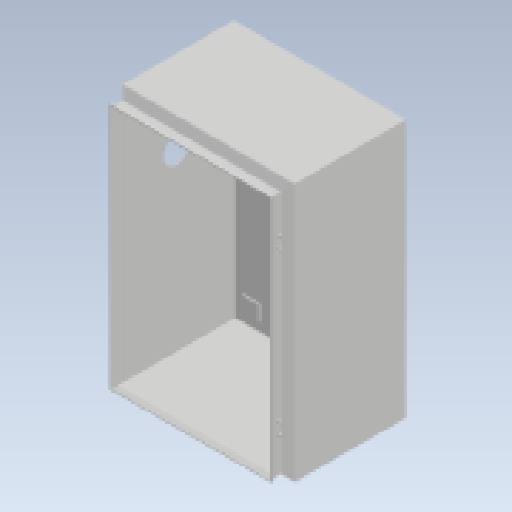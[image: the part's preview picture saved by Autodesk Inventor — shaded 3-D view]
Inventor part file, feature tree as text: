
AUTODESK INVENTOR PART (.ipt)
format: ipt  version: 2025.2 (Build 292293000, 293)  size: 891,392 bytes
history: native  units: mm
features: other x56, sketch x45, extrude x21, revolve x20, hole x4
ambient origin geometry x8: Origin, YZ Plane, XZ Plane, XY Plane, X Axis, Y Axis, Z Axis, Center Point
bodies: Solid1 (feature_tree)
feature tree (146):
  extrude  "Extrusion1"  Depth=300.0mm TaperAngle=0.0deg
  extrude  "Extrusion2"  Depth=300.0mm TaperAngle=0.0deg
  extrude  "Extrusion3"  Depth=3.25mm TaperAngle=0.0deg
  extrude  "Extrusion4"  Depth=3.25mm TaperAngle=0.0deg
  extrude  "Extrusion5"  Depth=15.297mm TaperAngle=0.0deg
  extrude  "Extrusion6"  Depth=15.297mm TaperAngle=0.0deg
  extrude  "Extrusion7"  Depth=15.297mm TaperAngle=0.0deg
  extrude  "Extrusion8"  Depth=15.297mm TaperAngle=0.0deg
  extrude  "Extrusion9"  TaperAngle=90.0deg  [1 undecoded]
  extrude  "Extrusion10"  TaperAngle=90.0deg  [1 undecoded]
  extrude  "Extrusion11"  TaperAngle=90.0deg  [1 undecoded]
  extrude  "Extrusion12"  TaperAngle=90.0deg  [1 undecoded]
  extrude  "Extrusion13"  TaperAngle=90.0deg  [1 undecoded]
  extrude  "Extrusion14"  TaperAngle=90.0deg  [1 undecoded]
  extrude  "Extrusion15"  TaperAngle=90.0deg  [1 undecoded]
  extrude  "Extrusion16"  TaperAngle=90.0deg  [1 undecoded]
  revolve  "Revolution1"  Angle=360.0deg
  revolve  "Revolution2"  Angle=360.0deg
  revolve  "Revolution3"  [1 undecoded]
  revolve  "Revolution4"  [1 undecoded]
  revolve  "Revolution5"  [1 undecoded]
  revolve  "Revolution6"  [1 undecoded]
  revolve  "Revolution7"  [1 undecoded]
  revolve  "Revolution8"  [1 undecoded]
  revolve  "Revolution9"  [1 undecoded]
  revolve  "Revolution10"  [1 undecoded]
  revolve  "Revolution11"  [1 undecoded]
  revolve  "Revolution12"  [1 undecoded]
  revolve  "Revolution13"  [1 undecoded]
  revolve  "Revolution14"  [1 undecoded]
  revolve  "Revolution15"  [1 undecoded]
  revolve  "Revolution16"  [1 undecoded]
  hole  "Hole1"  [1 undecoded]
  hole  "Hole2"  [1 undecoded]
  hole  "Hole3"  [1 undecoded]
  hole  "Hole4"  [1 undecoded]
  revolve  "Revolution17"  [1 undecoded]
  revolve  "Revolution18"  [1 undecoded]
  revolve  "Revolution19"  [1 undecoded]
  revolve  "Revolution20"  [1 undecoded]
  extrude  "Extrusion17"  [1 undecoded]
  extrude  "Extrusion18"  [1 undecoded]
  extrude  "Extrusion19"  [1 undecoded]
  extrude  "Extrusion20"  [1 undecoded]
  other  "GEHAEUSE_XY"
  other  "GEHAEUSE_YZ"
  other  "GEHAEUSE_ZX"
  other  "GEHAEUSE_X"
  other  "GEHAEUSE_Y"
  other  "GEHAEUSE_Z"
  other  "GEHAEUSE_Center"
  other  "to_HINGE_1_XY"
  other  "to_HINGE_1_YZ"
  other  "to_HINGE_1_ZX"
  other  "to_HINGE_1_X"
  other  "to_HINGE_1_Y"
  other  "to_HINGE_1_Z"
  other  "to_HINGE_1_Center"
  other  "to_HINGE_2_XY"
  other  "to_HINGE_2_YZ"
  other  "to_HINGE_2_ZX"
  other  "to_HINGE_2_X"
  other  "to_HINGE_2_Y"
  other  "to_HINGE_2_Z"
  other  "to_HINGE_2_Center"
  other  "to_L_Winkel_XY"
  other  "to_L_Winkel_YZ"
  other  "to_L_Winkel_ZX"
  other  "to_L_Winkel_X"
  other  "to_L_Winkel_Y"
  other  "to_L_Winkel_Z"
  other  "to_L_Winkel_Center"
  other  "to_L_Winkel_Bottom_XY"
  other  "to_L_Winkel_Bottom_YZ"
  other  "to_L_Winkel_Bottom_ZX"
  other  "to_L_Winkel_Bottom_X"
  other  "to_L_Winkel_Bottom_Y"
  other  "to_L_Winkel_Bottom_Z"
  other  "to_L_Winkel_Bottom_Center"
  other  "to_L_Winkel_Top_XY"
  other  "to_L_Winkel_Top_YZ"
  other  "to_L_Winkel_Top_ZX"
  other  "to_L_Winkel_Top_X"
  other  "to_L_Winkel_Top_Y"
  other  "to_L_Winkel_Top_Z"
  other  "to_L_Winkel_Top_Center"
  other  "to_L_Winkel_1_XY"
  other  "to_L_Winkel_1_YZ"
  other  "to_L_Winkel_1_ZX"
  other  "to_L_Winkel_1_X"
  other  "to_L_Winkel_1_Y"
  other  "to_L_Winkel_1_Z"
  other  "to_L_Winkel_1_Center"
  other  "to_MP_XY"
  other  "to_MP_YZ"
  other  "to_MP_ZX"
  other  "to_MP_X"
  other  "to_MP_Y"
  other  "to_MP_Z"
  other  "to_MP_Center"
  extrude  "Extrusão22"  [1 undecoded]
  sketch  "Skizze_2"  dims[d4=200.0mm d5=0.0mm d6=300.0mm d7=0.0mm]
  sketch  "Sketch_1"  dims[d0=200.0mm d1=0.0mm d2=300.0mm d3=0.0mm]
  sketch  "Sketch_37"  dims[d44=90.0deg d45=90.0deg]
  sketch  "Sketch_38"  dims[d46=90.0deg d47=90.0deg]
  sketch  "Sketch_2"  dims[d8=3.25mm d9=0.0mm d10=3.25mm d11=0.0mm]
  sketch  "Sketch_9"  dims[d12=3.25mm d13=0.0mm d14=3.25mm d15=0.0mm]
  sketch  "Sketch_10"  dims[d16=15.297mm d17=0.0mm d18=15.297mm d19=0.0mm]
  sketch  "Sketch_11"  dims[d20=15.297mm d21=0.0mm d22=15.297mm d23=0.0mm]
  sketch  "Sketch_30"  dims[d24=15.297mm d25=0.0mm d26=15.297mm d27=0.0mm]
  sketch  "Sketch_31"  dims[d28=15.297mm d29=0.0mm d30=15.297mm d31=0.0mm]
  sketch  "Sketch_32"  dims[d32=90.0deg d33=90.0deg]
  sketch  "Sketch_33"  dims[d34=90.0deg d35=90.0deg]
  sketch  "Sketch_43"  dims[d48=3.2mm d49=6.0mm d50=4.0mm d51=2.0mm d52=90.0deg d53=1.25mm d54=0.0mm]
  sketch  "Sketch_44"  dims[d55=3.2mm d56=6.0mm d57=4.0mm d58=2.0mm d59=90.0deg d60=1.25mm d61=0.0mm]
  sketch  "Sketch_45"  dims[d62=3.2mm d63=6.0mm d64=4.0mm d65=2.0mm d66=90.0deg d67=1.25mm d68=0.0mm]
  sketch  "Sketch_46"  dims[d69=3.2mm d70=6.0mm d71=4.0mm d72=2.0mm d73=90.0deg d74=1.25mm d75=0.0mm d76=360.0deg]
  sketch  "Sketch_47"  dims[d77=360.0deg d78=360.0deg]
  sketch  "Sketch_48"  dims[d82=1.2mm d83=0.0mm d84=1.2mm d85=0.0mm]
  sketch  "Sketch_49"  dims[d86=1.2mm d87=0.0mm d88=0.0mm]
  sketch  "Sketch_50"  dims[d89=0.0mm d90=0.0mm]
  sketch  "Sketch_51"  dims[d91=0.0mm d98=61.02mm]
  sketch  "Sketch_52"  dims[d99=10.0mm d100=0.0mm]
  sketch  "Sketch_53"
  sketch  "Sketch_54"
  sketch  "Sketch_55"
  sketch  "Sketch_56"
  sketch  "Sketch_57"
  sketch  "Sketch_58"
  sketch  "Sketch_59"
  sketch  "Sketch_60"
  sketch  "Sketch_61"
  sketch  "Sketch_62"
  sketch  "Sketch33"  dims[d36=90.0deg d37=90.0deg]
  sketch  "Sketch34"  dims[d38=90.0deg d39=90.0deg]
  sketch  "Sketch35"  dims[d40=90.0deg d41=90.0deg]
  sketch  "Sketch36"  dims[d42=90.0deg d43=90.0deg]
  sketch  "Sketch_75"
  sketch  "Sketch_76"
  sketch  "Sketch_77"
  sketch  "Sketch_78"
  sketch  "Sketch_79"
  sketch  "Sketch_80"
  sketch  "Sketch_81"
  sketch  "Sketch_82"
  sketch  "Esboço47"  dims[d79=360.0deg d80=1.2mm d81=0.0mm]
note: 35 required parameter values undecoded (feature->parameter linkage not recoverable at this tier; creation-order binding heuristic only, values carry confidence <= 0.55)